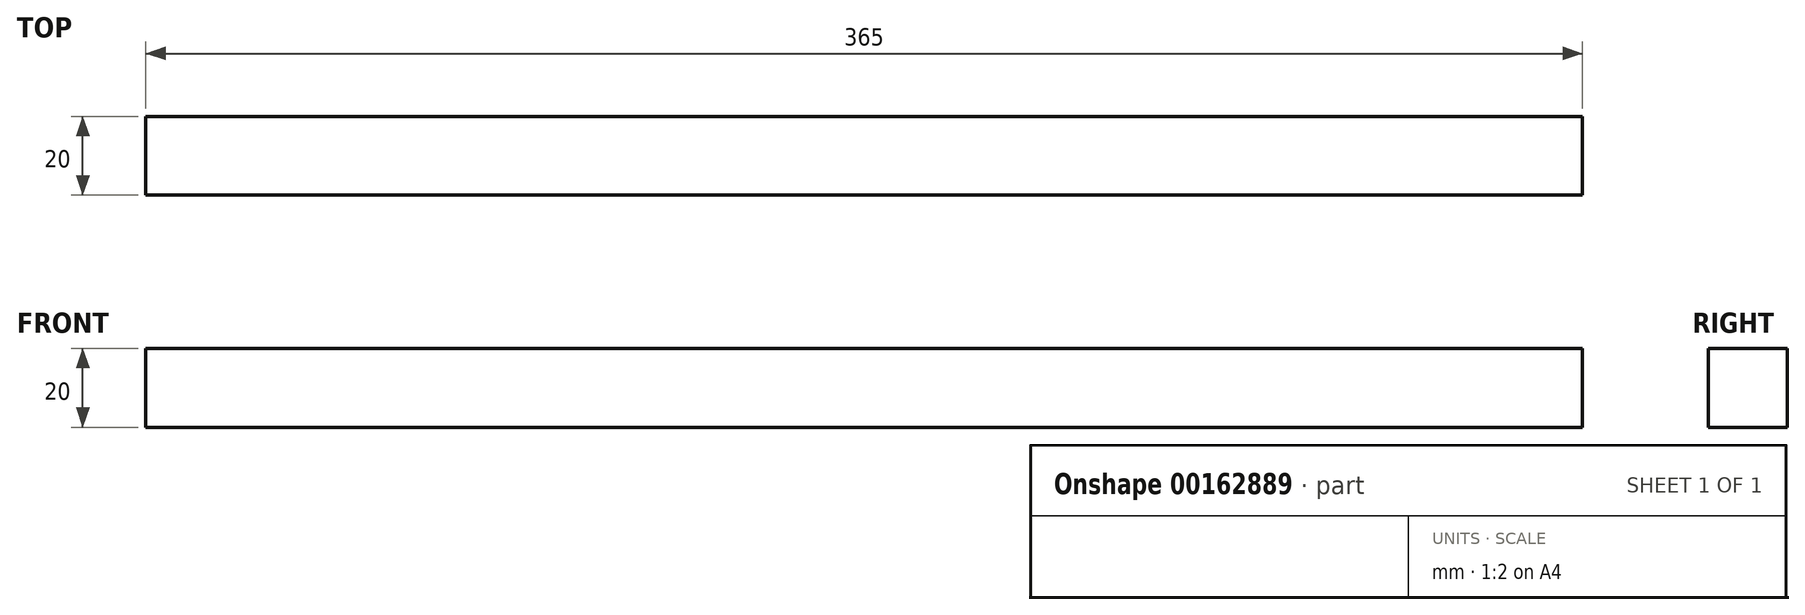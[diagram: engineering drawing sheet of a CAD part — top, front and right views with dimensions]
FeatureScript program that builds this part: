
annotation { "Feature Type Name" : "Feature", "Feature Type Description" : "" }
export const myFeature = defineFeature(function(context is Context, id is Id, definition is map)
    precondition{}
    {
        {
            var Q0;
            Q0=qCreatedBy(makeId("Right.planeOp"),FACE);
            var sketch = newSketch(context, id + "F0", { "sketchPlane" : qUnion([Q0])});
            skLineSegment(sketch, "E0.bottom", {"start": v(10, -10) * mm, "end": v(-10, -10) * mm});
            skLineSegment(sketch, "E0.top", {"start": v(10, 10) * mm, "end": v(-10, 10) * mm});
            skLineSegment(sketch, "E0.left", {"start": v(10, -10) * mm, "end": v(10, 10) * mm});
            skLineSegment(sketch, "E0.right", {"start": v(-10, -10) * mm, "end": v(-10, 10) * mm});
            skPoint(sketch, "E0.middle", {"position": v(0, 0) * mm});
            skSolve(sketch);
        }
        {
            var Q0;
            Q0=makeQuery(id+"F0.imprint","IMPRINT",FACE,{"disambiguationData":[TD([[makeQuery(id+"F0.imprint","IMPRINT",EDGE,{"derivedFrom":sQuery(id+"F0.wireOp",EDGE,"E0.bottom")}),-1.0]])]});
            extrude(context, id + "F1", {"entities" : qUnion([Q0]), "depth" : 365 * mm, "offsetDistance" : 25 * mm});
        }
    });
